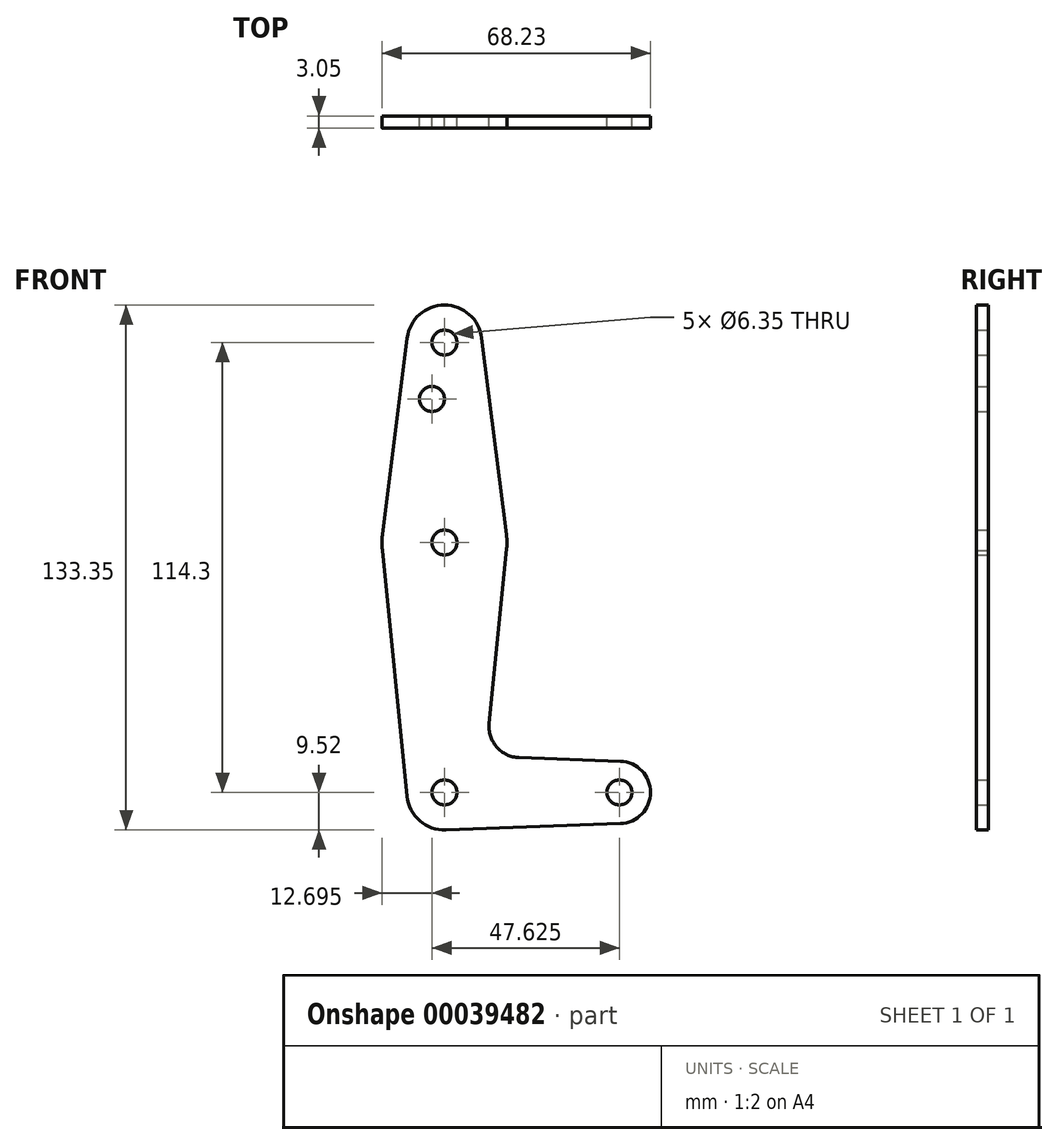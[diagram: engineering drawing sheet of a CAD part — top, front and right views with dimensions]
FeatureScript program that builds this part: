
annotation { "Feature Type Name" : "Feature", "Feature Type Description" : "" }
export const myFeature = defineFeature(function(context is Context, id is Id, definition is map)
    precondition{}
    {
        {
            var Q0;
            Q0=qCreatedBy(makeId("Front.planeOp"),FACE);
            var sketch = newSketch(context, id + "F0", { "sketchPlane" : qUnion([Q0])});
            skLineSegment(sketch, "E0", {"start": v(0, 0) * mm, "end": v(0, 114.3) * mm, "construction": true});
            skLineSegment(sketch, "E1", {"start": v(0, 0) * mm, "end": v(44.45, 0) * mm, "construction": true});
            skCircle(sketch, "E2", {"center": v(0, 114.3) * mm, "radius": 9.53 * mm});
            skCircle(sketch, "E3", {"center": v(0, 0) * mm, "radius": 9.53 * mm});
            skCircle(sketch, "E4", {"center": v(44.45, 0) * mm, "radius": 7.91 * mm});
            skCircle(sketch, "E5", {"center": v(0, 63.5) * mm, "radius": 15.88 * mm});
            skLineSegment(sketch, "E6", {"start": v(-9.45, 115.5) * mm, "end": v(-15.75, 65.48) * mm});
            skLineSegment(sketch, "E7", {"start": v(-9.48, -0.95) * mm, "end": v(-15.75, 61.52) * mm});
            skLineSegment(sketch, "E8", {"start": v(11.34, 17.58) * mm, "end": v(15.8, 61.91) * mm});
            skLineSegment(sketch, "E9", {"start": v(9.45, 115.5) * mm, "end": v(15.75, 65.48) * mm});
            skLineSegment(sketch, "E10", {"start": v(0, 63.5) * mm, "end": v(0, 0) * mm, "construction": true});
            skLineSegment(sketch, "E11", {"start": v(18.96, 8.84) * mm, "end": v(44.74, 7.9) * mm});
            skLineSegment(sketch, "E12", {"start": v(44.74, -7.9) * mm, "end": v(0, -9.53) * mm});
            skCircle(sketch, "E13", {"center": v(0, 114.3) * mm, "radius": 3.18 * mm});
            skCircle(sketch, "E14", {"center": v(0, 63.5) * mm, "radius": 3.18 * mm});
            skCircle(sketch, "E15", {"center": v(0, 0) * mm, "radius": 3.18 * mm});
            skCircle(sketch, "E16", {"center": v(44.45, 0) * mm, "radius": 3.18 * mm});
            skArc(sketch, "E17.filletArc", {"start": v(11.34, 17.58) * mm, "mid": v(13.26, 11.56) * mm, "end": v(18.96, 8.84) * mm});
            skCircle(sketch, "E18", {"center": v(-3.18, 99.96) * mm, "radius": 3.18 * mm});
            skSolve(sketch);
        }
        {
            var Q0;
            Q0=makeQuery(id+"F0.imprint","IMPRINT",FACE,{"disambiguationData":[TD([[makeQuery(id+"F0.imprint","IMPRINT",EDGE,{"derivedFrom":sQuery(id+"F0.wireOp",EDGE,"E13")}),-1.0]])]});
            var Q1;
            {var subQ2=sQuery(id+"F0.wireOp",EDGE,"E6");Q1=makeQuery(id+"F0.imprint","IMPRINT",FACE,{"disambiguationData":[TD([[makeQuery(id+"F0.imprint","IMPRINT",EDGE,{"derivedFrom":subQ2}),1.0]])]});}
            var Q2;
            Q2=makeQuery(id+"F0.imprint","IMPRINT",FACE,{"disambiguationData":[TD([[makeQuery(id+"F0.imprint","IMPRINT",EDGE,{"derivedFrom":sQuery(id+"F0.wireOp",EDGE,"E14")}),-1.0]])]});
            var Q3;
            {var subQ7=sQuery(id+"F0.wireOp",EDGE,"E7");Q3=makeQuery(id+"F0.imprint","IMPRINT",FACE,{"disambiguationData":[TD([[makeQuery(id+"F0.imprint","IMPRINT",EDGE,{"derivedFrom":subQ7}),-1.0]])]});}
            var Q4;
            Q4=makeQuery(id+"F0.imprint","IMPRINT",FACE,{"disambiguationData":[TD([[makeQuery(id+"F0.imprint","IMPRINT",EDGE,{"derivedFrom":sQuery(id+"F0.wireOp",EDGE,"E15")}),-1.0]])]});
            var Q5;
            Q5=makeQuery(id+"F0.imprint","IMPRINT",FACE,{"disambiguationData":[TD([[makeQuery(id+"F0.imprint","IMPRINT",EDGE,{"derivedFrom":sQuery(id+"F0.wireOp",EDGE,"E16")}),-1.0]])]});
            extrude(context, id + "F1", {"entities" : qUnion([Q0, Q1, Q2, Q3, Q4, Q5]), "depth" : 3.05 * mm});
        }
    });
